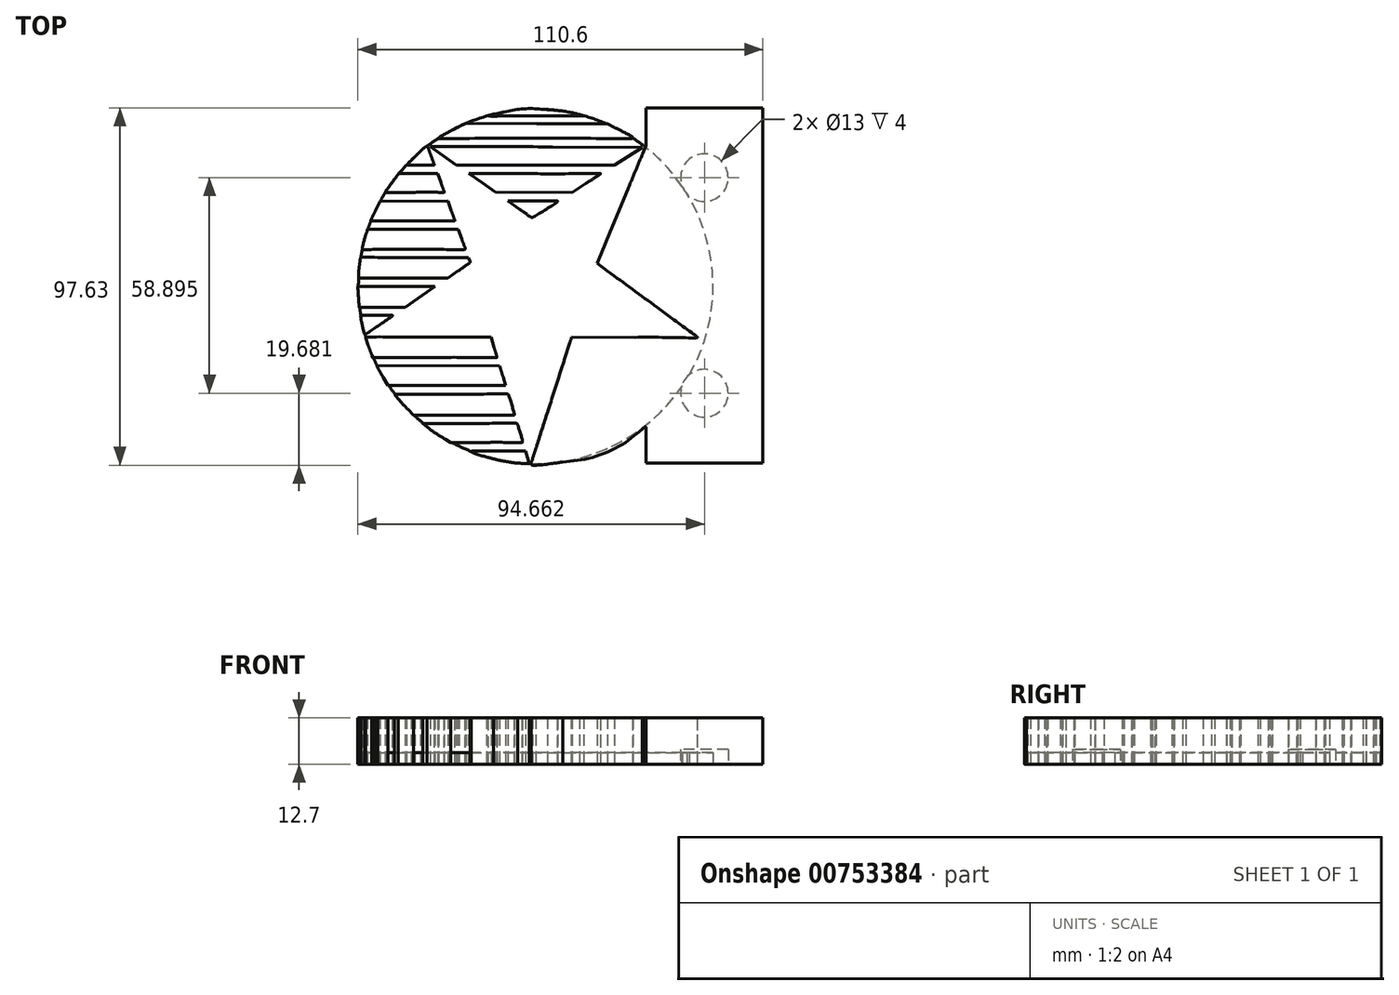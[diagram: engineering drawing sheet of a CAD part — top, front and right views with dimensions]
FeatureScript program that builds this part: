
annotation { "Feature Type Name" : "Feature", "Feature Type Description" : "" }
export const myFeature = defineFeature(function(context is Context, id is Id, definition is map)
    precondition{}
    {
        {
            var Q0;
            Q0=qCreatedBy(makeId("Top.planeOp"),FACE);
            var sketch = newSketch(context, id + "F0", { "sketchPlane" : qUnion([Q0])});
            skFitSpline(sketch, "E0", {"points": [v(-7.95, -48.52) * mm, v(-7.95, -48.43) * mm, v(-7.25, -46.2) * mm, v(-6.4, -43.56) * mm]});
            skFitSpline(sketch, "E1", {"points": [v(-6.4, -43.56) * mm, v(-5.55, -40.92) * mm, v(-4.14, -36.5) * mm, v(-3.25, -33.76) * mm]});
            skFitSpline(sketch, "E2", {"points": [v(-3.25, -33.76) * mm, v(-2.37, -31) * mm, v(-0.65, -25.66) * mm, v(0.56, -21.89) * mm]});
            skFitSpline(sketch, "E3", {"points": [v(0.56, -21.89) * mm, v(1.78, -18.1) * mm, v(2.85, -14.77) * mm, v(2.93, -14.48) * mm]});
            skLineSegment(sketch, "E4", {"start": v(2.93, -14.48) * mm, "end": v(3.08, -13.94) * mm});
            skLineSegment(sketch, "E5", {"start": v(3.08, -13.94) * mm, "end": v(20.33, -14.03) * mm});
            skFitSpline(sketch, "E6", {"points": [v(20.33, -14.03) * mm, v(32.43, -14.1) * mm, v(37.53, -14.07) * mm, v(37.41, -13.95) * mm]});
            skFitSpline(sketch, "E7", {"points": [v(37.41, -13.95) * mm, v(37.32, -13.85) * mm, v(32.4, -10.22) * mm, v(26.48, -5.87) * mm]});
            skFitSpline(sketch, "E8", {"points": [v(26.48, -5.87) * mm, v(20.55, -1.53) * mm, v(14.44, 2.97) * mm, v(12.88, 4.1) * mm]});
            skLineSegment(sketch, "E9", {"start": v(12.88, 4.1) * mm, "end": v(10.05, 6.19) * mm});
            skLineSegment(sketch, "E10", {"start": v(10.05, 6.19) * mm, "end": v(11.07, 8.64) * mm});
            skFitSpline(sketch, "E11", {"points": [v(11.07, 8.64) * mm, v(11.63, 10) * mm, v(12.8, 12.81) * mm, v(13.67, 14.91) * mm]});
            skFitSpline(sketch, "E12", {"points": [v(13.67, 14.91) * mm, v(14.54, 17) * mm, v(16.67, 22.16) * mm, v(18.41, 26.36) * mm]});
            skFitSpline(sketch, "E13", {"points": [v(18.41, 26.36) * mm, v(20.15, 30.55) * mm, v(22, 34.98) * mm, v(22.5, 36.2) * mm]});
            skLineSegment(sketch, "E14", {"start": v(22.5, 36.2) * mm, "end": v(23.42, 38.4) * mm});
            skLineSegment(sketch, "E15", {"start": v(23.42, 38.4) * mm, "end": v(23.42, 43.53) * mm});
            skLineSegment(sketch, "E16", {"start": v(23.42, 43.53) * mm, "end": v(23.42, 48.66) * mm});
            skLineSegment(sketch, "E17", {"start": v(23.42, 48.66) * mm, "end": v(39.36, 48.66) * mm});
            skLineSegment(sketch, "E18", {"start": v(39.36, 48.66) * mm, "end": v(55.3, 48.66) * mm});
            skLineSegment(sketch, "E19", {"start": v(55.3, 48.66) * mm, "end": v(55.3, 0.16) * mm});
            skLineSegment(sketch, "E20", {"start": v(55.3, 0.16) * mm, "end": v(55.3, -48.34) * mm});
            skLineSegment(sketch, "E21", {"start": v(55.3, -48.34) * mm, "end": v(39.36, -48.34) * mm});
            skLineSegment(sketch, "E22", {"start": v(39.36, -48.34) * mm, "end": v(23.42, -48.34) * mm});
            skLineSegment(sketch, "E23", {"start": v(23.42, -48.34) * mm, "end": v(23.42, -43.42) * mm});
            skFitSpline(sketch, "E24", {"points": [v(23.42, -43.42) * mm, v(23.42, -40.72) * mm, v(23.36, -38.5) * mm, v(23.28, -38.5) * mm]});
            skFitSpline(sketch, "E25", {"points": [v(23.28, -38.5) * mm, v(23.2, -38.5) * mm, v(22.8, -38.76) * mm, v(22.38, -39.08) * mm]});
            skFitSpline(sketch, "E26", {"points": [v(22.38, -39.08) * mm, v(16.6, -43.49) * mm, v(8.22, -46.97) * mm, v(0.7, -48.07) * mm]});
            skFitSpline(sketch, "E27", {"points": [v(0.7, -48.07) * mm, v(-2.64, -48.56) * mm, v(-7.95, -48.84) * mm, v(-7.95, -48.52) * mm]});
            skLineSegment(sketch, "E28", {"start": v(-7.95, -48.52) * mm, "end": v(-7.95, -48.52) * mm});
            skFitSpline(sketch, "E29", {"points": [v(-11.6, -48.39) * mm, v(-13.04, -48.25) * mm, v(-16.56, -47.63) * mm, v(-18.2, -47.23) * mm]});
            skFitSpline(sketch, "E30", {"points": [v(-18.2, -47.23) * mm, v(-19.97, -46.78) * mm, v(-23.95, -45.53) * mm, v(-24.4, -45.27) * mm]});
            skFitSpline(sketch, "E31", {"points": [v(-24.4, -45.27) * mm, v(-24.54, -45.2) * mm, v(-21.4, -45.13) * mm, v(-17.1, -45.12) * mm]});
            skLineSegment(sketch, "E32", {"start": v(-17.1, -45.12) * mm, "end": v(-9.53, -45.12) * mm});
            skLineSegment(sketch, "E33", {"start": v(-9.53, -45.12) * mm, "end": v(-9.01, -46.81) * mm});
            skLineSegment(sketch, "E34", {"start": v(-9.01, -46.81) * mm, "end": v(-8.5, -48.5) * mm});
            skLineSegment(sketch, "E35", {"start": v(-8.5, -48.5) * mm, "end": v(-9.7, -48.48) * mm});
            skFitSpline(sketch, "E36", {"points": [v(-9.7, -48.48) * mm, v(-10.37, -48.46) * mm, v(-11.22, -48.42) * mm, v(-11.6, -48.39) * mm]});
            skLineSegment(sketch, "E37", {"start": v(-11.6, -48.39) * mm, "end": v(-11.6, -48.39) * mm});
            skFitSpline(sketch, "E38", {"points": [v(-31.34, -41.88) * mm, v(-33.33, -40.68) * mm, v(-35.14, -39.46) * mm, v(-36.43, -38.44) * mm]});
            skLineSegment(sketch, "E39", {"start": v(-36.43, -38.44) * mm, "end": v(-37.52, -37.57) * mm});
            skLineSegment(sketch, "E40", {"start": v(-37.52, -37.57) * mm, "end": v(-24.74, -37.53) * mm});
            skFitSpline(sketch, "E41", {"points": [v(-24.74, -37.53) * mm, v(-17.7, -37.5) * mm, v(-11.9, -37.54) * mm, v(-11.84, -37.61) * mm]});
            skFitSpline(sketch, "E42", {"points": [v(-11.84, -37.61) * mm, v(-11.73, -37.75) * mm, v(-10.31, -42.4) * mm, v(-10.32, -42.62) * mm]});
            skFitSpline(sketch, "E43", {"points": [v(-10.32, -42.62) * mm, v(-10.32, -42.69) * mm, v(-14.73, -42.74) * mm, v(-20.11, -42.74) * mm]});
            skLineSegment(sketch, "E44", {"start": v(-20.11, -42.74) * mm, "end": v(-29.9, -42.74) * mm});
            skLineSegment(sketch, "E45", {"start": v(-29.9, -42.74) * mm, "end": v(-31.34, -41.88) * mm});
            skLineSegment(sketch, "E46", {"start": v(-31.34, -41.88) * mm, "end": v(-31.34, -41.88) * mm});
            skFitSpline(sketch, "E47", {"points": [v(-41.63, -33.71) * mm, v(-42.48, -32.85) * mm, v(-43.65, -31.57) * mm, v(-44.23, -30.87) * mm]});
            skLineSegment(sketch, "E48", {"start": v(-44.23, -30.87) * mm, "end": v(-45.28, -29.6) * mm});
            skLineSegment(sketch, "E49", {"start": v(-45.28, -29.6) * mm, "end": v(-29.8, -29.56) * mm});
            skFitSpline(sketch, "E50", {"points": [v(-29.8, -29.56) * mm, v(-21.3, -29.53) * mm, v(-14.3, -29.55) * mm, v(-14.26, -29.6) * mm]});
            skFitSpline(sketch, "E51", {"points": [v(-14.26, -29.6) * mm, v(-14.2, -29.66) * mm, v(-12.53, -35.07) * mm, v(-12.53, -35.22) * mm]});
            skFitSpline(sketch, "E52", {"points": [v(-12.53, -35.22) * mm, v(-12.53, -35.25) * mm, v(-18.73, -35.28) * mm, v(-26.3, -35.28) * mm]});
            skLineSegment(sketch, "E53", {"start": v(-26.3, -35.28) * mm, "end": v(-40.09, -35.28) * mm});
            skLineSegment(sketch, "E54", {"start": v(-40.09, -35.28) * mm, "end": v(-41.63, -33.71) * mm});
            skFitSpline(sketch, "E55", {"points": [v(-48.34, -24.98) * mm, v(-49.05, -23.8) * mm, v(-49.75, -22.57) * mm, v(-49.9, -22.27) * mm]});
            skLineSegment(sketch, "E56", {"start": v(-49.9, -22.27) * mm, "end": v(-50.18, -21.71) * mm});
            skLineSegment(sketch, "E57", {"start": v(-50.18, -21.71) * mm, "end": v(-33.36, -21.76) * mm});
            skLineSegment(sketch, "E58", {"start": v(-33.36, -21.76) * mm, "end": v(-16.54, -21.8) * mm});
            skLineSegment(sketch, "E59", {"start": v(-16.54, -21.8) * mm, "end": v(-16.42, -22.23) * mm});
            skFitSpline(sketch, "E60", {"points": [v(-16.42, -22.23) * mm, v(-16.35, -22.46) * mm, v(-16, -23.66) * mm, v(-15.62, -24.9) * mm]});
            skLineSegment(sketch, "E61", {"start": v(-15.62, -24.9) * mm, "end": v(-14.94, -27.14) * mm});
            skLineSegment(sketch, "E62", {"start": v(-14.94, -27.14) * mm, "end": v(-31, -27.14) * mm});
            skLineSegment(sketch, "E63", {"start": v(-31, -27.14) * mm, "end": v(-47.06, -27.14) * mm});
            skLineSegment(sketch, "E64", {"start": v(-47.06, -27.14) * mm, "end": v(-48.34, -24.98) * mm});
            skFitSpline(sketch, "E65", {"points": [v(-51.46, -18.88) * mm, v(-51.61, -18.53) * mm, v(-52.07, -17.3) * mm, v(-52.47, -16.17) * mm]});
            skLineSegment(sketch, "E66", {"start": v(-52.47, -16.17) * mm, "end": v(-53.21, -14.1) * mm});
            skLineSegment(sketch, "E67", {"start": v(-53.21, -14.1) * mm, "end": v(-52.67, -14) * mm});
            skFitSpline(sketch, "E68", {"points": [v(-52.67, -14) * mm, v(-52.37, -13.95) * mm, v(-44.65, -13.93) * mm, v(-35.51, -13.95) * mm]});
            skLineSegment(sketch, "E69", {"start": v(-35.51, -13.95) * mm, "end": v(-18.9, -14) * mm});
            skLineSegment(sketch, "E70", {"start": v(-18.9, -14) * mm, "end": v(-18.1, -16.71) * mm});
            skFitSpline(sketch, "E71", {"points": [v(-18.1, -16.71) * mm, v(-17.65, -18.2) * mm, v(-17.28, -19.45) * mm, v(-17.28, -19.47) * mm]});
            skFitSpline(sketch, "E72", {"points": [v(-17.28, -19.47) * mm, v(-17.28, -19.5) * mm, v(-24.9, -19.51) * mm, v(-34.23, -19.51) * mm]});
            skLineSegment(sketch, "E73", {"start": v(-34.23, -19.51) * mm, "end": v(-51.18, -19.51) * mm});
            skLineSegment(sketch, "E74", {"start": v(-51.18, -19.51) * mm, "end": v(-51.46, -18.88) * mm});
            skFitSpline(sketch, "E75", {"points": [v(-53.44, -13.12) * mm, v(-53.54, -12.96) * mm, v(-54.34, -9.52) * mm, v(-54.49, -8.62) * mm]});
            skLineSegment(sketch, "E76", {"start": v(-54.49, -8.62) * mm, "end": v(-54.6, -7.98) * mm});
            skLineSegment(sketch, "E77", {"start": v(-54.6, -7.98) * mm, "end": v(-50.15, -7.98) * mm});
            skFitSpline(sketch, "E78", {"points": [v(-50.15, -7.98) * mm, v(-47.53, -7.98) * mm, v(-45.76, -8.04) * mm, v(-45.86, -8.13) * mm]});
            skFitSpline(sketch, "E79", {"points": [v(-45.86, -8.13) * mm, v(-46.01, -8.28) * mm, v(-52, -12.39) * mm, v(-52.91, -12.97) * mm]});
            skFitSpline(sketch, "E80", {"points": [v(-52.91, -12.97) * mm, v(-53.16, -13.13) * mm, v(-53.4, -13.2) * mm, v(-53.44, -13.12) * mm]});
            skFitSpline(sketch, "E81", {"points": [v(-54.98, -4.89) * mm, v(-55.03, -4.4) * mm, v(-55.13, -3.14) * mm, v(-55.2, -2.09) * mm]});
            skLineSegment(sketch, "E82", {"start": v(-55.2, -2.09) * mm, "end": v(-55.3, -0.18) * mm});
            skLineSegment(sketch, "E83", {"start": v(-55.3, -0.18) * mm, "end": v(-44.74, -0.18) * mm});
            skLineSegment(sketch, "E84", {"start": v(-44.74, -0.18) * mm, "end": v(-34.18, -0.18) * mm});
            skLineSegment(sketch, "E85", {"start": v(-34.18, -0.18) * mm, "end": v(-38.27, -2.98) * mm});
            skLineSegment(sketch, "E86", {"start": v(-38.27, -2.98) * mm, "end": v(-42.36, -5.78) * mm});
            skLineSegment(sketch, "E87", {"start": v(-42.36, -5.78) * mm, "end": v(-48.62, -5.78) * mm});
            skLineSegment(sketch, "E88", {"start": v(-48.62, -5.78) * mm, "end": v(-54.88, -5.78) * mm});
            skLineSegment(sketch, "E89", {"start": v(-54.88, -5.78) * mm, "end": v(-54.98, -4.89) * mm});
            skFitSpline(sketch, "E90", {"points": [v(-55.09, 3.08) * mm, v(-55.08, 3.57) * mm, v(-54.97, 4.81) * mm, v(-54.83, 5.84) * mm]});
            skFitSpline(sketch, "E91", {"points": [v(-54.83, 5.84) * mm, v(-54.7, 6.86) * mm, v(-54.58, 7.72) * mm, v(-54.58, 7.75) * mm]});
            skFitSpline(sketch, "E92", {"points": [v(-54.58, 7.75) * mm, v(-54.58, 7.77) * mm, v(-47.94, 7.79) * mm, v(-39.83, 7.79) * mm]});
            skLineSegment(sketch, "E93", {"start": v(-39.83, 7.79) * mm, "end": v(-25.08, 7.79) * mm});
            skLineSegment(sketch, "E94", {"start": v(-25.08, 7.79) * mm, "end": v(-24.82, 7.16) * mm});
            skFitSpline(sketch, "E95", {"points": [v(-24.82, 7.16) * mm, v(-24.6, 6.66) * mm, v(-24.6, 6.5) * mm, v(-24.77, 6.32) * mm]});
            skFitSpline(sketch, "E96", {"points": [v(-24.77, 6.32) * mm, v(-24.9, 6.2) * mm, v(-26.28, 5.23) * mm, v(-27.86, 4.15) * mm]});
            skLineSegment(sketch, "E97", {"start": v(-27.86, 4.15) * mm, "end": v(-30.74, 2.2) * mm});
            skLineSegment(sketch, "E98", {"start": v(-30.74, 2.2) * mm, "end": v(-42.91, 2.2) * mm});
            skLineSegment(sketch, "E99", {"start": v(-42.91, 2.2) * mm, "end": v(-55.09, 2.2) * mm});
            skLineSegment(sketch, "E100", {"start": v(-55.09, 2.2) * mm, "end": v(-55.09, 3.08) * mm});
            skFitSpline(sketch, "E101", {"points": [v(-54.07, 10.2) * mm, v(-54.07, 10.5) * mm, v(-53.14, 13.98) * mm, v(-52.84, 14.83) * mm]});
            skLineSegment(sketch, "E102", {"start": v(-52.84, 14.83) * mm, "end": v(-52.6, 15.5) * mm});
            skLineSegment(sketch, "E103", {"start": v(-52.6, 15.5) * mm, "end": v(-40.25, 15.5) * mm});
            skLineSegment(sketch, "E104", {"start": v(-40.25, 15.5) * mm, "end": v(-27.9, 15.5) * mm});
            skLineSegment(sketch, "E105", {"start": v(-27.9, 15.5) * mm, "end": v(-26.92, 12.88) * mm});
            skFitSpline(sketch, "E106", {"points": [v(-26.92, 12.88) * mm, v(-26.38, 11.43) * mm, v(-25.94, 10.2) * mm, v(-25.93, 10.12) * mm]});
            skFitSpline(sketch, "E107", {"points": [v(-25.93, 10.12) * mm, v(-25.93, 10.05) * mm, v(-32.26, 10) * mm, v(-40, 10) * mm]});
            skFitSpline(sketch, "E108", {"points": [v(-40, 10) * mm, v(-51.14, 10) * mm, v(-54.07, 10.04) * mm, v(-54.07, 10.2) * mm]});
            skFitSpline(sketch, "E109", {"points": [v(-51.6, 18.18) * mm, v(-51.54, 18.39) * mm, v(-50.98, 19.59) * mm, v(-50.36, 20.85) * mm]});
            skLineSegment(sketch, "E110", {"start": v(-50.36, 20.85) * mm, "end": v(-49.24, 23.14) * mm});
            skLineSegment(sketch, "E111", {"start": v(-49.24, 23.14) * mm, "end": v(-39.98, 23.18) * mm});
            skLineSegment(sketch, "E112", {"start": v(-39.98, 23.18) * mm, "end": v(-30.71, 23.22) * mm});
            skLineSegment(sketch, "E113", {"start": v(-30.71, 23.22) * mm, "end": v(-29.76, 20.59) * mm});
            skFitSpline(sketch, "E114", {"points": [v(-29.76, 20.59) * mm, v(-29.23, 19.13) * mm, v(-28.8, 17.91) * mm, v(-28.8, 17.87) * mm]});
            skFitSpline(sketch, "E115", {"points": [v(-28.8, 17.87) * mm, v(-28.8, 17.83) * mm, v(-33.96, 17.8) * mm, v(-40.26, 17.8) * mm]});
            skLineSegment(sketch, "E116", {"start": v(-40.26, 17.8) * mm, "end": v(-51.72, 17.8) * mm});
            skLineSegment(sketch, "E117", {"start": v(-51.72, 17.8) * mm, "end": v(-51.6, 18.18) * mm});
            skLineSegment(sketch, "E118", {"start": v(-11.07, 20.95) * mm, "end": v(-14.27, 23.22) * mm});
            skLineSegment(sketch, "E119", {"start": v(-14.27, 23.22) * mm, "end": v(-7.43, 23.22) * mm});
            skFitSpline(sketch, "E120", {"points": [v(-7.43, 23.22) * mm, v(-3.64, 23.22) * mm, v(-0.66, 23.16) * mm, v(-0.75, 23.08) * mm]});
            skFitSpline(sketch, "E121", {"points": [v(-0.75, 23.08) * mm, v(-1.05, 22.8) * mm, v(-7.37, 18.83) * mm, v(-7.62, 18.75) * mm]});
            skFitSpline(sketch, "E122", {"points": [v(-7.62, 18.75) * mm, v(-7.75, 18.7) * mm, v(-9.3, 19.7) * mm, v(-11.07, 20.95) * mm]});
            skFitSpline(sketch, "E123", {"points": [v(-47.27, 26.4) * mm, v(-46.98, 26.84) * mm, v(-46.15, 27.99) * mm, v(-45.44, 28.94) * mm]});
            skLineSegment(sketch, "E124", {"start": v(-45.44, 28.94) * mm, "end": v(-44.15, 30.68) * mm});
            skLineSegment(sketch, "E125", {"start": v(-44.15, 30.68) * mm, "end": v(-38.81, 30.68) * mm});
            skLineSegment(sketch, "E126", {"start": v(-38.81, 30.68) * mm, "end": v(-33.47, 30.68) * mm});
            skLineSegment(sketch, "E127", {"start": v(-33.47, 30.68) * mm, "end": v(-32.63, 28.35) * mm});
            skFitSpline(sketch, "E128", {"points": [v(-32.63, 28.35) * mm, v(-32.18, 27.07) * mm, v(-31.77, 25.92) * mm, v(-31.73, 25.8) * mm]});
            skFitSpline(sketch, "E129", {"points": [v(-31.73, 25.8) * mm, v(-31.67, 25.64) * mm, v(-33.34, 25.6) * mm, v(-39.73, 25.6) * mm]});
            skLineSegment(sketch, "E130", {"start": v(-39.73, 25.6) * mm, "end": v(-47.81, 25.6) * mm});
            skLineSegment(sketch, "E131", {"start": v(-47.81, 25.6) * mm, "end": v(-47.27, 26.4) * mm});
            skLineSegment(sketch, "E132", {"start": v(-47.27, 26.4) * mm, "end": v(-47.27, 26.4) * mm});
            skLineSegment(sketch, "E133", {"start": v(-21.32, 28.14) * mm, "end": v(-24.95, 30.68) * mm});
            skLineSegment(sketch, "E134", {"start": v(-24.95, 30.68) * mm, "end": v(-6.92, 30.68) * mm});
            skFitSpline(sketch, "E135", {"points": [v(-6.92, 30.68) * mm, v(2.99, 30.68) * mm, v(11.07, 30.65) * mm, v(11.03, 30.62) * mm]});
            skFitSpline(sketch, "E136", {"points": [v(11.03, 30.62) * mm, v(11, 30.58) * mm, v(9.22, 29.44) * mm, v(7.1, 28.07) * mm]});
            skLineSegment(sketch, "E137", {"start": v(7.1, 28.07) * mm, "end": v(3.23, 25.6) * mm});
            skLineSegment(sketch, "E138", {"start": v(3.23, 25.6) * mm, "end": v(-7.24, 25.6) * mm});
            skLineSegment(sketch, "E139", {"start": v(-7.24, 25.6) * mm, "end": v(-17.7, 25.6) * mm});
            skLineSegment(sketch, "E140", {"start": v(-17.7, 25.6) * mm, "end": v(-21.32, 28.14) * mm});
            skLineSegment(sketch, "E141", {"start": v(-21.32, 28.14) * mm, "end": v(-21.32, 28.14) * mm});
            skFitSpline(sketch, "E142", {"points": [v(-40.67, 34.34) * mm, v(-38.96, 36.08) * mm, v(-36.42, 38.2) * mm, v(-36.27, 38.03) * mm]});
            skFitSpline(sketch, "E143", {"points": [v(-36.27, 38.03) * mm, v(-36.2, 37.95) * mm, v(-35.78, 36.9) * mm, v(-35.33, 35.68) * mm]});
            skFitSpline(sketch, "E144", {"points": [v(-35.33, 35.68) * mm, v(-34.89, 34.47) * mm, v(-34.49, 33.38) * mm, v(-34.44, 33.27) * mm]});
            skFitSpline(sketch, "E145", {"points": [v(-34.44, 33.27) * mm, v(-34.38, 33.1) * mm, v(-35.2, 33.06) * mm, v(-38.15, 33.06) * mm]});
            skLineSegment(sketch, "E146", {"start": v(-38.15, 33.06) * mm, "end": v(-41.94, 33.06) * mm});
            skLineSegment(sketch, "E147", {"start": v(-41.94, 33.06) * mm, "end": v(-40.67, 34.34) * mm});
            skLineSegment(sketch, "E148", {"start": v(-31.93, 35.57) * mm, "end": v(-35.49, 38.06) * mm});
            skLineSegment(sketch, "E149", {"start": v(-35.49, 38.06) * mm, "end": v(-31, 38.1) * mm});
            skFitSpline(sketch, "E150", {"points": [v(-31, 38.1) * mm, v(-28.53, 38.12) * mm, v(-15.5, 38.08) * mm, v(-2.06, 38.01) * mm]});
            skLineSegment(sketch, "E151", {"start": v(-2.06, 38.01) * mm, "end": v(22.4, 37.89) * mm});
            skLineSegment(sketch, "E152", {"start": v(22.4, 37.89) * mm, "end": v(18.62, 35.47) * mm});
            skLineSegment(sketch, "E153", {"start": v(18.62, 35.47) * mm, "end": v(14.84, 33.06) * mm});
            skLineSegment(sketch, "E154", {"start": v(14.84, 33.06) * mm, "end": v(-6.77, 33.06) * mm});
            skLineSegment(sketch, "E155", {"start": v(-6.77, 33.06) * mm, "end": v(-28.38, 33.07) * mm});
            skLineSegment(sketch, "E156", {"start": v(-28.38, 33.07) * mm, "end": v(-31.93, 35.57) * mm});
            skLineSegment(sketch, "E157", {"start": v(-31.93, 35.57) * mm, "end": v(-31.93, 35.57) * mm});
            skFitSpline(sketch, "E158", {"points": [v(-33.2, 40.42) * mm, v(-32.91, 40.7) * mm, v(-29.21, 42.76) * mm, v(-27.65, 43.5) * mm]});
            skLineSegment(sketch, "E159", {"start": v(-27.65, 43.5) * mm, "end": v(-25.74, 44.42) * mm});
            skLineSegment(sketch, "E160", {"start": v(-25.74, 44.42) * mm, "end": v(-6.46, 44.38) * mm});
            skLineSegment(sketch, "E161", {"start": v(-6.46, 44.38) * mm, "end": v(12.82, 44.33) * mm});
            skLineSegment(sketch, "E162", {"start": v(12.82, 44.33) * mm, "end": v(14.72, 43.37) * mm});
            skFitSpline(sketch, "E163", {"points": [v(14.72, 43.37) * mm, v(16.72, 42.36) * mm, v(19.86, 40.56) * mm, v(19.86, 40.43) * mm]});
            skFitSpline(sketch, "E164", {"points": [v(19.86, 40.43) * mm, v(19.86, 40.38) * mm, v(7.9, 40.35) * mm, v(-6.7, 40.35) * mm]});
            skFitSpline(sketch, "E165", {"points": [v(-6.7, 40.35) * mm, v(-21.32, 40.35) * mm, v(-33.24, 40.38) * mm, v(-33.2, 40.42) * mm]});
            skFitSpline(sketch, "E166", {"points": [v(-19.63, 46.52) * mm, v(-19.6, 46.56) * mm, v(-18.5, 46.82) * mm, v(-17.19, 47.1) * mm]});
            skFitSpline(sketch, "E167", {"points": [v(-17.19, 47.1) * mm, v(-12.57, 48.1) * mm, v(-7.82, 48.47) * mm, v(-3.48, 48.16) * mm]});
            skFitSpline(sketch, "E168", {"points": [v(-3.48, 48.16) * mm, v(-0.65, 47.96) * mm, v(3.19, 47.36) * mm, v(5.2, 46.8) * mm]});
            skLineSegment(sketch, "E169", {"start": v(5.2, 46.8) * mm, "end": v(6.38, 46.48) * mm});
            skLineSegment(sketch, "E170", {"start": v(6.38, 46.48) * mm, "end": v(-6.66, 46.47) * mm});
            skFitSpline(sketch, "E171", {"points": [v(-6.66, 46.47) * mm, v(-13.84, 46.46) * mm, v(-19.67, 46.48) * mm, v(-19.63, 46.52) * mm]});
            skLineSegment(sketch, "E172", {"start": v(-19.63, 46.52) * mm, "end": v(-19.63, 46.52) * mm});
            skSolve(sketch);
        }
        {
            var Q0;
            Q0 = qSketchRegion(id + "F0", true);
            extrude(context, id + "F1", {"entities" : qUnion([Q0]), "depth" : 12.7 * mm, "offsetDistance" : 25.4 * mm});
        }
        {
            var Q0;
            Q0=qCreatedBy(makeId("Top.planeOp"),FACE);
            var sketch = newSketch(context, id + "F2", { "sketchPlane" : qUnion([Q0])});
            skCircle(sketch, "E173", {"center": v(-6.7, -0.1) * mm, "radius": 48.42 * mm});
            skPoint(sketch, "E173.first.point", {"position": v(-54.74, 6.04) * mm});
            skPoint(sketch, "E173.second.point", {"position": v(7.3, -46.45) * mm});
            skPoint(sketch, "E173.third.point", {"position": v(18.44, 41.28) * mm});
            skCircle(sketch, "E174", {"center": v(39.36, -29.29) * mm, "radius": 6.5 * mm});
            skCircle(sketch, "E175", {"center": v(39.36, 29.6) * mm, "radius": 6.5 * mm});
            skLineSegment(sketch, "E176", {"start": v(39.36, -48.34) * mm, "end": v(39.36, 48.87) * mm, "construction": true});
            skSolve(sketch);
        }
        {
            var Q0;
            Q0=makeQuery(id+"F2.imprint","IMPRINT",FACE,{"disambiguationData":[TD([[makeQuery(id+"F2.imprint","IMPRINT",EDGE,{"derivedFrom":sQuery(id+"F2.wireOp",EDGE,"E173")}),1.0]])]});
            var Q1;
            Q1=sQuery(id+"F2.wireOp",EDGE,"E173");
            extrude(context, id + "F3", {"entities" : qUnion([Q0]), "surfaceEntities" : qUnion([Q1]), "depth" : 3.17 * mm, "offsetDistance" : 25.4 * mm});
        }
        {
            var Q0;
            Q0=makeQuery(id+"F2.imprint","IMPRINT",FACE,{"disambiguationData":[TD([[makeQuery(id+"F2.imprint","IMPRINT",EDGE,{"derivedFrom":sQuery(id+"F2.wireOp",EDGE,"E174")}),1.0]])]});
            var Q1;
            Q1=makeQuery(id+"F2.imprint","IMPRINT",FACE,{"disambiguationData":[TD([[makeQuery(id+"F2.imprint","IMPRINT",EDGE,{"derivedFrom":sQuery(id+"F2.wireOp",EDGE,"E175")}),1.0]])]});
            extrude(context, id + "F4", {"entities" : qUnion([Q0, Q1]), "operationType" : NewBodyOperationType.REMOVE, "depth" : 4 * mm, "offsetDistance" : 25.4 * mm});
        }
    });
